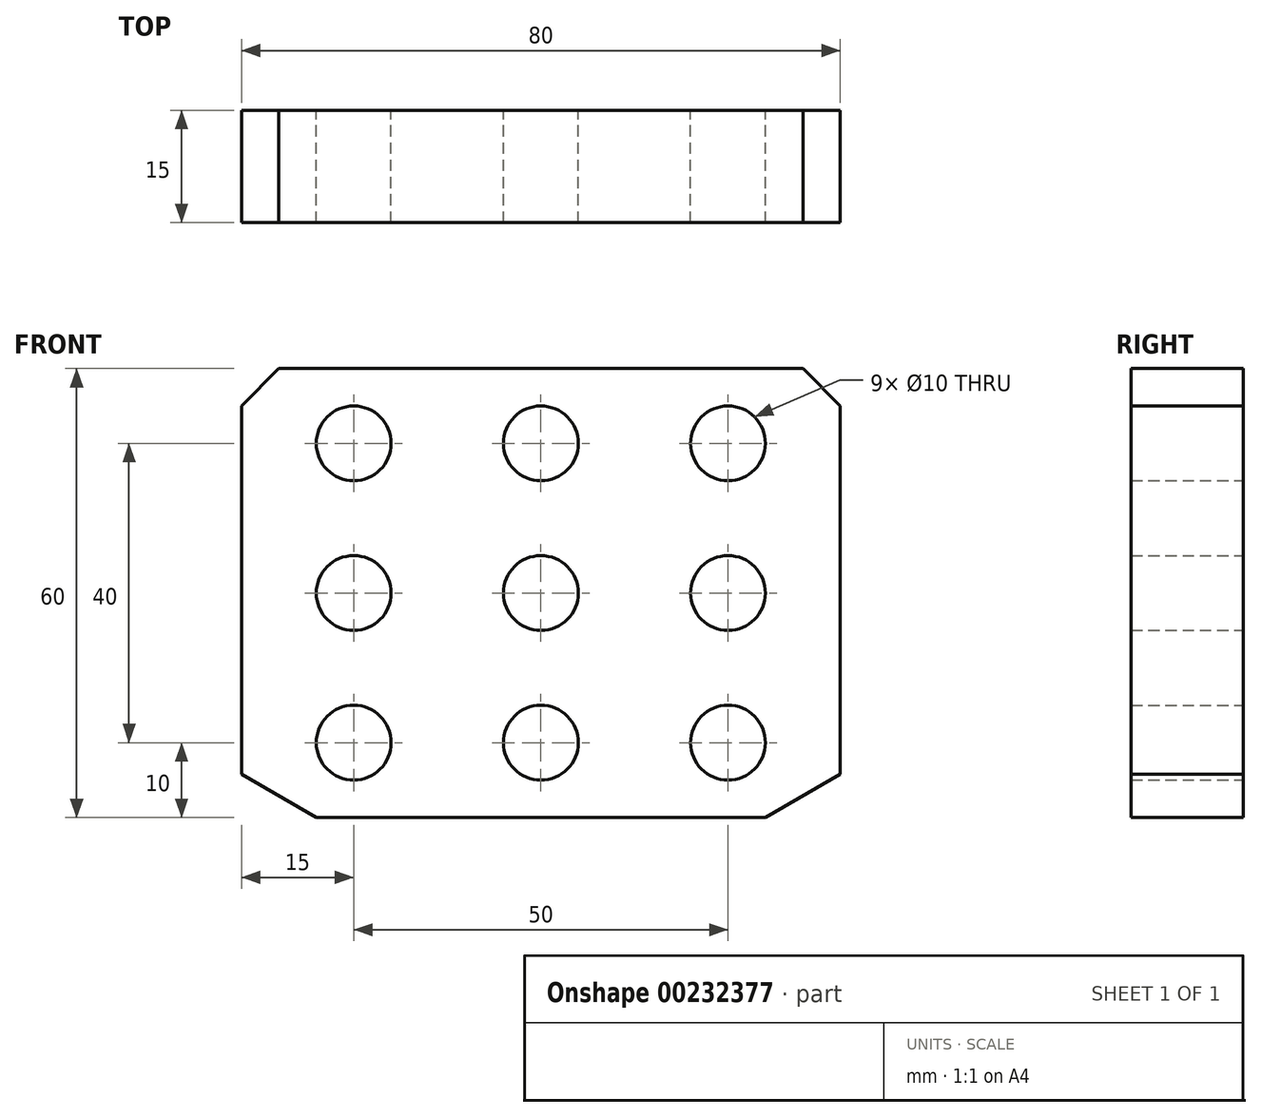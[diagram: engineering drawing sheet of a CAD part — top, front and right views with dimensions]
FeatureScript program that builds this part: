
annotation { "Feature Type Name" : "Feature", "Feature Type Description" : "" }
export const myFeature = defineFeature(function(context is Context, id is Id, definition is map)
    precondition{}
    {
        {
            var Q0;
            Q0=qCreatedBy(makeId("Front.planeOp"),FACE);
            var sketch = newSketch(context, id + "F0", { "sketchPlane" : qUnion([Q0])});
            skLineSegment(sketch, "E0", {"start": v(0, 30) * mm, "end": v(35, 30) * mm});
            skLineSegment(sketch, "E1", {"start": v(35, 30) * mm, "end": v(40, 25) * mm});
            skLineSegment(sketch, "E2", {"start": v(40, 25) * mm, "end": v(40, -24.23) * mm});
            skLineSegment(sketch, "E3", {"start": v(40, -24.23) * mm, "end": v(30, -30) * mm});
            skLineSegment(sketch, "E4", {"start": v(30, -30) * mm, "end": v(0, -30) * mm});
            skLineSegment(sketch, "E5", {"start": v(-25, -12.62) * mm, "end": v(-25, -27) * mm, "construction": true});
            skLineSegment(sketch, "E6", {"start": v(-32.24, -20) * mm, "end": v(-15.83, -20) * mm, "construction": true});
            skCircle(sketch, "E7", {"center": v(-25, -20) * mm, "radius": 5 * mm});
            skCircle(sketch, "E8.0.1.0", {"center": v(-25, 0) * mm, "radius": 5 * mm});
            skCircle(sketch, "E8.0.2.0", {"center": v(-25, 20) * mm, "radius": 5 * mm});
            skCircle(sketch, "E8.1.0.0", {"center": v(0, -20) * mm, "radius": 5 * mm});
            skCircle(sketch, "E8.1.1.0", {"center": v(0, 0) * mm, "radius": 5 * mm});
            skCircle(sketch, "E8.1.2.0", {"center": v(0, 20) * mm, "radius": 5 * mm});
            skCircle(sketch, "E8.2.0.0", {"center": v(25, -20) * mm, "radius": 5 * mm});
            skCircle(sketch, "E8.2.1.0", {"center": v(25, 0) * mm, "radius": 5 * mm});
            skCircle(sketch, "E8.2.2.0", {"center": v(25, 20) * mm, "radius": 5 * mm});
            skLineSegment(sketch, "E8.direction1", {"start": v(-25, -20) * mm, "end": v(0, -20) * mm, "construction": true});
            skLineSegment(sketch, "E8.direction2", {"start": v(-25, -20) * mm, "end": v(-25, 0) * mm, "construction": true});
            skLineSegment(sketch, "E9.MirrorCS", {"start": v(-30, -30) * mm, "end": v(0, -30) * mm});
            skLineSegment(sketch, "E10.MirrorCS", {"start": v(-40, -24.23) * mm, "end": v(-30, -30) * mm});
            skLineSegment(sketch, "E11.MirrorCS", {"start": v(-40, 25) * mm, "end": v(-40, -24.23) * mm});
            skLineSegment(sketch, "E12.MirrorCS", {"start": v(-35, 30) * mm, "end": v(-40, 25) * mm});
            skLineSegment(sketch, "E13.MirrorCS", {"start": v(0, 30) * mm, "end": v(-35, 30) * mm});
            skSolve(sketch);
        }
        {
            var Q0;
            Q0=makeQuery(id+"F0.imprint","IMPRINT",FACE,{"disambiguationData":[TD([[makeQuery(id+"F0.imprint","IMPRINT",EDGE,{"derivedFrom":sQuery(id+"F0.wireOp",EDGE,"E0")}),-1.0]])]});
            extrude(context, id + "F1", {"entities" : qUnion([Q0]), "depth" : 15 * mm});
        }
    });
